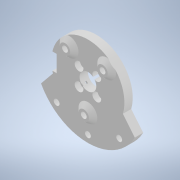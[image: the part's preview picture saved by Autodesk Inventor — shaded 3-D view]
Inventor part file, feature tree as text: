
AUTODESK INVENTOR PART (.ipt)
format: ipt  version: 2021 (Build 250183000, 183)  size: 229,376 bytes
history: native  units: mm
features: projected_geometry x7, extrude x4, sketch x4, chamfer x1
ambient origin geometry x8: Origin, YZ Plane, XZ Plane, XY Plane, X Axis, Y Axis, Z Axis, Center Point
bodies: Solid1 (feature_tree)
feature tree (16):
  extrude  "Extrusion1"  Depth=8.0mm
  extrude  "Extrusion2"  Depth=4.0mm
  extrude  "Extrusion3"  Depth=4.0mm
  chamfer  "Chamfer1"  Distance=2.5mm
  extrude  "Extrusion4"  Depth=4.0mm
  sketch  "Sketch1"  dims[d0=35.0mm d1=8.0mm]
  sketch  "Sketch2"  dims[d4=4.0mm d5=0.0mm]
  projected_geometry  "Projected Loop1"
  projected_geometry  "Projected Loop2"
  projected_geometry  "Projected Loop3"
  projected_geometry  "Projected Loop4"
  sketch  "Sketch3"  dims[d6=8.0mm d7=2.4mm d8=8.5mm d9=8.5mm d10=4.25mm d11=4.25mm]
  projected_geometry  "Projected Loop5"
  projected_geometry  "Projected Loop6"
  projected_geometry  "Projected Loop7"
  sketch  "Sketch4"  dims[d12=23.0mm d13=18.0mm d14=2.8mm d15=5.0mm d16=13.0mm d17=9.0mm d18=4.2mm d19=2.5mm d20=0.0mm d21=5.0mm d22=2.0mm d23=0.0mm d24=2.0mm d25=2.0mm d26=45.0deg d27=12.0mm d28=5.0mm d29=22.0mm d30=2.8mm d32=15.0mm d33=22.0mm d34=22.0mm d35=15.0mm d36=4.0mm d37=8.0mm d38=33.0mm d41=30.0deg d42=3.0mm d43=2.0mm d44=0.0mm]
